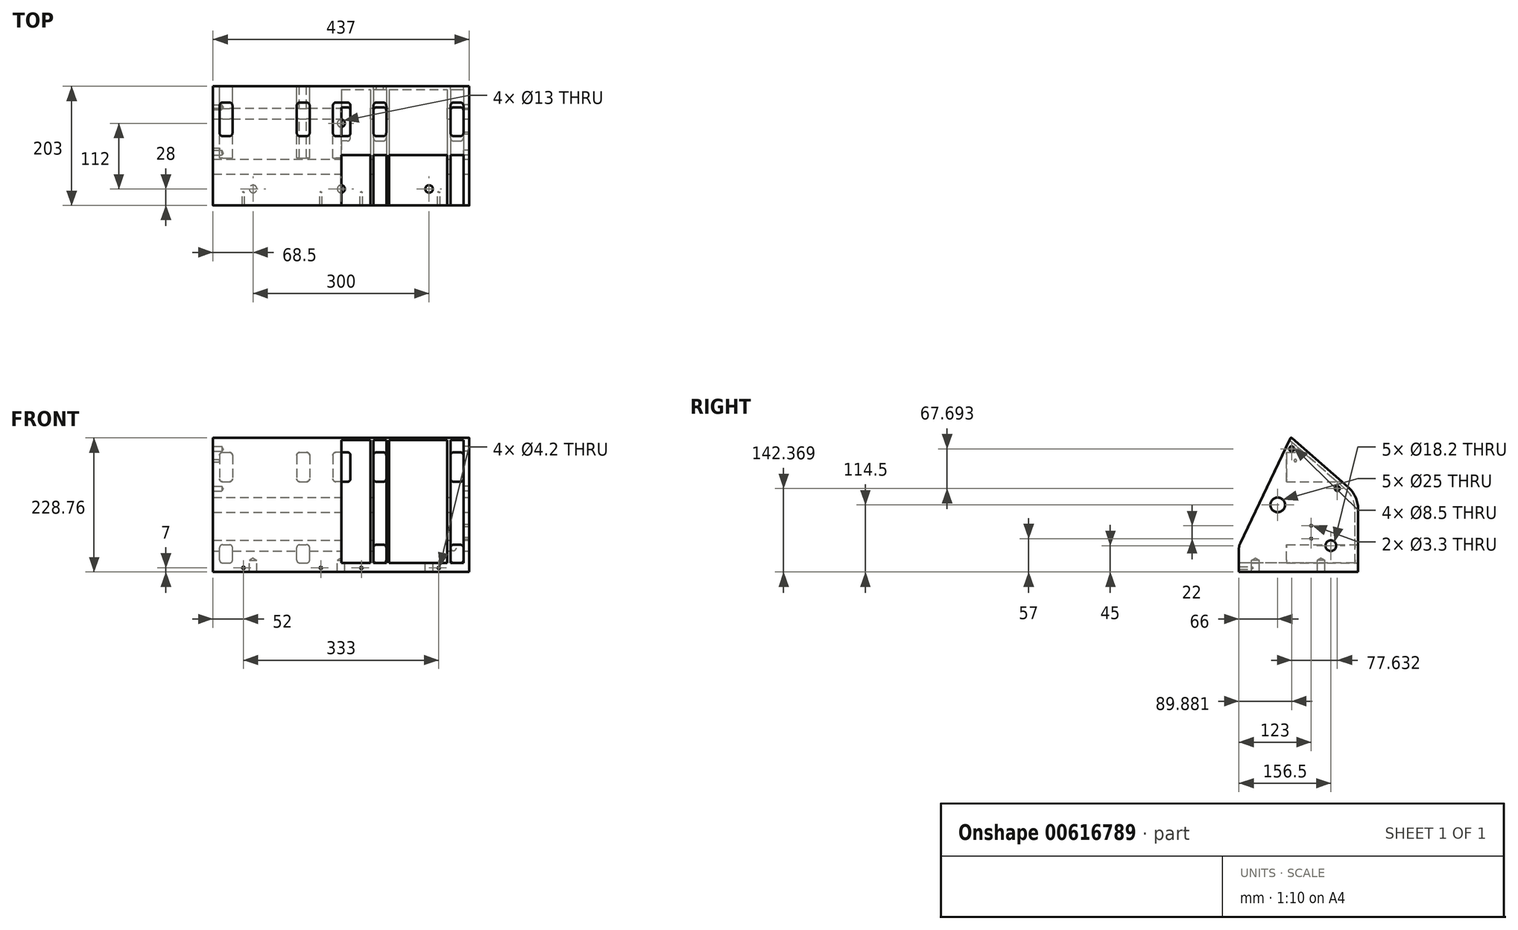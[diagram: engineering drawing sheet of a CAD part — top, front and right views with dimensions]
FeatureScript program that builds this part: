
annotation { "Feature Type Name" : "Feature", "Feature Type Description" : "" }
export const myFeature = defineFeature(function(context is Context, id is Id, definition is map)
    precondition{}
    {
        {
            var Q0;
            Q0=qCreatedBy(makeId("Right.planeOp"),FACE);
            var sketch = newSketch(context, id + "F0", { "sketchPlane" : qUnion([Q0])});
            skLineSegment(sketch, "E0", {"start": v(0, 0) * mm, "end": v(-203, 0) * mm});
            skLineSegment(sketch, "E1", {"start": v(-203, 0) * mm, "end": v(-203, 40.47) * mm});
            skLineSegment(sketch, "E2", {"start": v(0, 0) * mm, "end": v(0, 107.26) * mm});
            skLineSegment(sketch, "E3", {"start": v(-17.14, 144.95) * mm, "end": v(-112.7, 228.27) * mm});
            skLineSegment(sketch, "E4", {"start": v(-115.82, 227.62) * mm, "end": v(-201.05, 49.09) * mm});
            skPoint(sketch, "E5.visualSharp", {"position": v(0, 130) * mm});
            skArc(sketch, "E5.filletArc", {"start": v(0, 107.26) * mm, "mid": v(-4.49, 127.96) * mm, "end": v(-17.14, 144.95) * mm});
            skPoint(sketch, "E6.visualSharp", {"position": v(-203, 45) * mm});
            skArc(sketch, "E6.filletArc", {"start": v(-201.05, 49.09) * mm, "mid": v(-202.5, 44.89) * mm, "end": v(-203, 40.47) * mm});
            skPoint(sketch, "E7.visualSharp", {"position": v(-114.68, 230) * mm});
            skArc(sketch, "E7.filletArc", {"start": v(-112.7, 228.27) * mm, "mid": v(-114.42, 228.72) * mm, "end": v(-115.82, 227.62) * mm});
            skSolve(sketch);
        }
        {
            var Q0;
            Q0 = qSketchRegion(id + "F0", true);
            extrude(context, id + "F1", {"entities" : qUnion([Q0]), "oppositeDirection" : true, "depth" : 437 * mm, "offsetDistance" : 25 * mm});
        }
        {
            var Q0;
            Q0=makeQuery(id+"F1.opExtrude","CAP_FACE",FACE,{"disambiguationData":[OSD([sQuery(id+"F0.wireOp",EDGE,"E0"),sQuery(id+"F0.wireOp",EDGE,"E1"),sQuery(id+"F0.wireOp",EDGE,"E2"),sQuery(id+"F0.wireOp",EDGE,"E3"),sQuery(id+"F0.wireOp",EDGE,"E4"),sQuery(id+"F0.wireOp",EDGE,"E5.filletArc"),sQuery(id+"F0.wireOp",EDGE,"E6.filletArc"),sQuery(id+"F0.wireOp",EDGE,"E7.filletArc")])],"isStart":true});
            var sketch = newSketch(context, id + "F2", { "sketchPlane" : qUnion([Q0])});
            skLineSegment(sketch, "E8.0.0", {"start": v(-203, 0) * mm, "end": v(0, 0) * mm, "construction": true});
            skLineSegment(sketch, "E8.0.1", {"start": v(0, 0) * mm, "end": v(0, 107.26) * mm, "construction": true});
            skArc(sketch, "E8.0.2", {"start": v(0, 107.26) * mm, "mid": v(-4.49, 127.96) * mm, "end": v(-17.14, 144.95) * mm, "construction": true});
            skLineSegment(sketch, "E8.0.3", {"start": v(-17.14, 144.95) * mm, "end": v(-112.7, 228.27) * mm, "construction": true});
            skArc(sketch, "E8.0.4", {"start": v(-112.7, 228.27) * mm, "mid": v(-114.42, 228.72) * mm, "end": v(-115.82, 227.62) * mm, "construction": true});
            skLineSegment(sketch, "E8.0.5", {"start": v(-115.82, 227.62) * mm, "end": v(-201.05, 49.09) * mm, "construction": true});
            skArc(sketch, "E8.0.6", {"start": v(-201.05, 49.09) * mm, "mid": v(-202.5, 44.89) * mm, "end": v(-203, 40.47) * mm, "construction": true});
            skLineSegment(sketch, "E8.0.7", {"start": v(-203, 40.47) * mm, "end": v(-203, 0) * mm, "construction": true});
            skLineSegment(sketch, "E9.0", {"start": v(-197.5, 40.47) * mm, "end": v(-197.5, 15.5) * mm, "construction": true});
            skArc(sketch, "E9.1", {"start": v(-196.09, 46.72) * mm, "mid": v(-197.14, 43.67) * mm, "end": v(-197.5, 40.47) * mm, "construction": true});
            skLineSegment(sketch, "E9.2", {"start": v(-5.5, 5.5) * mm, "end": v(-5.5, 15.5) * mm, "construction": true});
            skArc(sketch, "E9.3", {"start": v(-5.5, 107.26) * mm, "mid": v(-9.5, 125.68) * mm, "end": v(-20.75, 140.8) * mm});
            skLineSegment(sketch, "E9.4", {"start": v(-20.75, 140.8) * mm, "end": v(-121.05, 228.26) * mm});
            skLineSegment(sketch, "E9.5", {"start": v(-197.5, 5.5) * mm, "end": v(-5.5, 5.5) * mm, "construction": true});
            skLineSegment(sketch, "E9.6", {"start": v(-112.84, 221.1) * mm, "end": v(-196.09, 46.72) * mm, "construction": true});
            skLineSegment(sketch, "E10", {"start": v(-197.5, 15.5) * mm, "end": v(-5.5, 15.5) * mm});
            skLineSegment(sketch, "E11", {"start": v(-197.5, 15.5) * mm, "end": v(-197.5, 5.5) * mm, "construction": true});
            skLineSegment(sketch, "E12", {"start": v(-5.5, 15.5) * mm, "end": v(-5.5, 107.26) * mm});
            skLineSegment(sketch, "E13.0", {"start": v(-208, 40.47) * mm, "end": v(-208, 15.5) * mm});
            skArc(sketch, "E13.1", {"start": v(-205.56, 51.24) * mm, "mid": v(-207.38, 46) * mm, "end": v(-208, 40.47) * mm});
            skLineSegment(sketch, "E13.2", {"start": v(-121.05, 228.26) * mm, "end": v(-205.56, 51.24) * mm});
            skLineSegment(sketch, "E14", {"start": v(-197.5, 15.5) * mm, "end": v(-208, 15.5) * mm});
            skLineSegment(sketch, "E15", {"start": v(-208, 15.5) * mm, "end": v(-208, 0) * mm, "construction": true});
            skSolve(sketch);
        }
        {
            var Q0;
            Q0 = qSketchRegion(id + "F2", true);
            extrude(context, id + "F3", {"entities" : qUnion([Q0]), "operationType" : NewBodyOperationType.REMOVE, "oppositeDirection" : true, "depth" : 32 * mm, "offsetDistance" : 25 * mm, "hasSecondDirection" : true, "secondDirectionOppositeDirection" : true, "secondDirectionDepth" : 10 * mm});
        }
        {
            var Q0;
            Q0 = qSketchRegion(id + "F2", true);
            extrude(context, id + "F4", {"entities" : qUnion([Q0]), "operationType" : NewBodyOperationType.REMOVE, "oppositeDirection" : true, "depth" : (((437 - (5 * 6) - 20 - (22 * 4)) / 3) + 15 + 22) * mm, "offsetDistance" : 25 * mm, "hasSecondDirection" : true, "secondDirectionOppositeDirection" : true, "secondDirectionDepth" : 38 * mm});
        }
        {
            var Q0;
            Q0 = qSketchRegion(id + "F2", true);
            extrude(context, id + "F5", {"entities" : qUnion([Q0]), "operationType" : NewBodyOperationType.REMOVE, "oppositeDirection" : true, "depth" : (141.5 + 22) * mm, "offsetDistance" : 25 * mm, "hasSecondDirection" : true, "secondDirectionOppositeDirection" : true, "secondDirectionDepth" : (10 + 23 + 5 + 98.5 + 5) * mm});
        }
        {
            var Q0;
            Q0 = qSketchRegion(id + "F2", true);
            extrude(context, id + "F6", {"entities" : qUnion([Q0]), "operationType" : NewBodyOperationType.REMOVE, "oppositeDirection" : true, "depth" : (163.5 + 5 + 98.67 / 2) * mm, "offsetDistance" : 25 * mm, "hasSecondDirection" : true, "secondDirectionOppositeDirection" : true, "secondDirectionDepth" : (163.5 + 5) * mm});
        }
        {
            var Q0;
            Q0=makeQuery(id+"F1.opExtrude","CAP_FACE",FACE,{"disambiguationData":[OSD([sQuery(id+"F0.wireOp",EDGE,"E0"),sQuery(id+"F0.wireOp",EDGE,"E1"),sQuery(id+"F0.wireOp",EDGE,"E2"),sQuery(id+"F0.wireOp",EDGE,"E3"),sQuery(id+"F0.wireOp",EDGE,"E4"),sQuery(id+"F0.wireOp",EDGE,"E5.filletArc"),sQuery(id+"F0.wireOp",EDGE,"E6.filletArc"),sQuery(id+"F0.wireOp",EDGE,"E7.filletArc")])],"isStart":true});
            var sketch = newSketch(context, id + "F7", { "sketchPlane" : qUnion([Q0])});
            skCircle(sketch, "E16", {"center": v(-46.5, 45) * mm, "radius": 9.1 * mm});
            skCircle(sketch, "E17", {"center": v(-137, 114.5) * mm, "radius": 12.5 * mm});
            skCircle(sketch, "E18", {"center": v(-80, 79) * mm, "radius": 2 * mm, "construction": true});
            skCircle(sketch, "E19", {"center": v(-80, 57) * mm, "radius": 2 * mm, "construction": true});
            skLineSegment(sketch, "E20", {"start": v(-80, 79) * mm, "end": v(-80, 57) * mm, "construction": true});
            skLineSegment(sketch, "E21", {"start": v(-80, 68) * mm, "end": v(0, 68) * mm, "construction": true});
            skSolve(sketch);
        }
        {
            var Q0;
            Q0=makeQuery(id+"F7.imprint","IMPRINT",FACE,{"disambiguationData":[TD([[makeQuery(id+"F7.imprint","IMPRINT",EDGE,{"derivedFrom":sQuery(id+"F7.wireOp",EDGE,"E17")}),1.0]])]});
            var Q1;
            Q1=makeQuery(id+"F7.imprint","IMPRINT",FACE,{"disambiguationData":[TD([[makeQuery(id+"F7.imprint","IMPRINT",EDGE,{"derivedFrom":sQuery(id+"F7.wireOp",EDGE,"E16")}),1.0]])]});
            extrude(context, id + "F8", {"entities" : qUnion([Q0, Q1]), "operationType" : NewBodyOperationType.REMOVE, "endBound" : BoundingType.THROUGH_ALL, "oppositeDirection" : true, "depth" : 25 * mm, "offsetDistance" : 25 * mm});
        }
        {
            var Q0;
            Q0=makeQuery(id+"F1.opExtrude","CAP_FACE",FACE,{"disambiguationData":[OSD([sQuery(id+"F0.wireOp",EDGE,"E0"),sQuery(id+"F0.wireOp",EDGE,"E1"),sQuery(id+"F0.wireOp",EDGE,"E2"),sQuery(id+"F0.wireOp",EDGE,"E3"),sQuery(id+"F0.wireOp",EDGE,"E4"),sQuery(id+"F0.wireOp",EDGE,"E5.filletArc"),sQuery(id+"F0.wireOp",EDGE,"E6.filletArc"),sQuery(id+"F0.wireOp",EDGE,"E7.filletArc")])],"isStart":false});
            var sketch = newSketch(context, id + "F9", { "sketchPlane" : qUnion([Q0])});
            skPoint(sketch, "E22", {"position": v(107, 190) * mm});
            skPoint(sketch, "E23", {"position": v(113.12, 210.06) * mm});
            skPoint(sketch, "E24", {"position": v(35.49, 142.37) * mm});
            skSolve(sketch);
        }
        {
            var Q0;
            Q0=makeQuery(id+"F1.opExtrude","CAP_FACE",FACE,{"disambiguationData":[OSD([sQuery(id+"F0.wireOp",EDGE,"E0"),sQuery(id+"F0.wireOp",EDGE,"E1"),sQuery(id+"F0.wireOp",EDGE,"E2"),sQuery(id+"F0.wireOp",EDGE,"E3"),sQuery(id+"F0.wireOp",EDGE,"E4"),sQuery(id+"F0.wireOp",EDGE,"E5.filletArc"),sQuery(id+"F0.wireOp",EDGE,"E6.filletArc"),sQuery(id+"F0.wireOp",EDGE,"E7.filletArc")])],"isStart":true});
            var sketch = newSketch(context, id + "F10", { "sketchPlane" : qUnion([Q0])});
            skPoint(sketch, "E25.0", {"position": v(-113.12, 210.06) * mm});
            skPoint(sketch, "E26.0", {"position": v(-35.49, 142.37) * mm});
            skSolve(sketch);
        }
        {
            var Q0;
            Q0=sQuery(id+"F7.wireOp",VERTEX,"E20.start");
            var Q1;
            Q1=sQuery(id+"F7.wireOp",VERTEX,"E20.end");
            var Q2;
            Q2=makeQuery(id+"F1.opExtrude","SWEPT_BODY",BODY,{"disambiguationData":[OSD([sQuery(id+"F0.wireOp",EDGE,"E0"),sQuery(id+"F0.wireOp",EDGE,"E1"),sQuery(id+"F0.wireOp",EDGE,"E2"),sQuery(id+"F0.wireOp",EDGE,"E3"),sQuery(id+"F0.wireOp",EDGE,"E4"),sQuery(id+"F0.wireOp",EDGE,"E5.filletArc"),sQuery(id+"F0.wireOp",EDGE,"E6.filletArc"),sQuery(id+"F0.wireOp",EDGE,"E7.filletArc")])]});
            hole(context, id + "F11", {"style" : HoleStyle.SIMPLE, "endStyle" : HoleEndStyle.BLIND, "standardTappedOrClearance" : lookupTablePath({ "standard" : "ISO", "engagement" : "75%", "pitch" : "0.7 mm", "size" : "M4", "type" : "Tapped" }), "standardBlindInLast" : lookupTablePath({ "standard" : "ISO", "fit" : "Normal", "engagement" : "75%", "pitch" : "0.7 mm", "size" : "M4", "type" : "Clearance & tapped" }), "holeDiameter" : 3.3 * mm, "majorDiameter" : 4 * mm, "showTappedDepth" : true, "holeDepth" : 14.1 * mm, "isTappedThrough" : true, "tappedDepth" : 12 * mm, "tapClearance" : 3, "locations" : qUnion([Q0, Q1]), "scope" : qUnion([Q2]), "startStyle" : HoleStartStyle.PART});
        }
        {
            var Q0;
            Q0=sQuery(id+"F9.wireOp",VERTEX,"E22");
            var Q1;
            Q1=makeQuery(id+"F1.opExtrude","SWEPT_BODY",BODY,{"disambiguationData":[OSD([sQuery(id+"F0.wireOp",EDGE,"E0"),sQuery(id+"F0.wireOp",EDGE,"E1"),sQuery(id+"F0.wireOp",EDGE,"E2"),sQuery(id+"F0.wireOp",EDGE,"E3"),sQuery(id+"F0.wireOp",EDGE,"E4"),sQuery(id+"F0.wireOp",EDGE,"E5.filletArc"),sQuery(id+"F0.wireOp",EDGE,"E6.filletArc"),sQuery(id+"F0.wireOp",EDGE,"E7.filletArc")])]});
            hole(context, id + "F12", {"style" : HoleStyle.SIMPLE, "endStyle" : HoleEndStyle.BLIND, "standardTappedOrClearance" : lookupTablePath({ "standard" : "ISO", "engagement" : "75%", "pitch" : "0.8 mm", "size" : "M5", "type" : "Tapped" }), "standardBlindInLast" : lookupTablePath({ "standard" : "ISO", "fit" : "Normal", "engagement" : "75%", "pitch" : "0.8 mm", "size" : "M5", "type" : "Clearance & tapped" }), "holeDiameter" : 4.2 * mm, "majorDiameter" : 5 * mm, "showTappedDepth" : true, "holeDepth" : 14.4 * mm, "isTappedThrough" : true, "tappedDepth" : 12 * mm, "tapClearance" : 3, "locations" : qUnion([Q0]), "scope" : qUnion([Q1]), "startStyle" : HoleStartStyle.PART});
        }
        {
            var Q0;
            Q0=sQuery(id+"F9.wireOp",VERTEX,"E24");
            var Q1;
            Q1=sQuery(id+"F9.wireOp",VERTEX,"E23");
            var Q2;
            Q2=sQuery(id+"F10.wireOp",VERTEX,"E26.0");
            var Q3;
            Q3=sQuery(id+"F10.wireOp",VERTEX,"E25.0");
            var Q4;
            Q4=makeQuery(id+"F1.opExtrude","SWEPT_BODY",BODY,{"disambiguationData":[OSD([sQuery(id+"F0.wireOp",EDGE,"E0"),sQuery(id+"F0.wireOp",EDGE,"E1"),sQuery(id+"F0.wireOp",EDGE,"E2"),sQuery(id+"F0.wireOp",EDGE,"E3"),sQuery(id+"F0.wireOp",EDGE,"E4"),sQuery(id+"F0.wireOp",EDGE,"E5.filletArc"),sQuery(id+"F0.wireOp",EDGE,"E6.filletArc"),sQuery(id+"F0.wireOp",EDGE,"E7.filletArc")])]});
            hole(context, id + "F13", {"style" : HoleStyle.SIMPLE, "endStyle" : HoleEndStyle.BLIND, "holeDiameter" : 8.5 * mm, "majorDiameter" : 5 * mm, "holeDepth" : 15 * mm, "isTappedThrough" : true, "tappedDepth" : 12 * mm, "tapClearance" : 3, "locations" : qUnion([Q0, Q1, Q2, Q3]), "scope" : qUnion([Q4]), "startStyle" : HoleStartStyle.PART});
        }
        {
            var Q0;
            Q0=makeQuery(id+"F1.opExtrude","SWEPT_FACE",FACE,{"disambiguationData":[OSD([sQuery(id+"F0.wireOp",EDGE,"E1")])]});
            var sketch = newSketch(context, id + "F14", { "sketchPlane" : qUnion([Q0])});
            skPoint(sketch, "E27", {"position": v(-385, 7) * mm});
            skPoint(sketch, "E28", {"position": v(-253, 7) * mm});
            skPoint(sketch, "E29", {"position": v(-184, 7) * mm});
            skPoint(sketch, "E30", {"position": v(-52, 7) * mm});
            skSolve(sketch);
        }
        {
            var Q0;
            Q0=sQuery(id+"F14.wireOp",VERTEX,"E27");
            var Q1;
            Q1=sQuery(id+"F14.wireOp",VERTEX,"E28");
            var Q2;
            Q2=sQuery(id+"F14.wireOp",VERTEX,"E29");
            var Q3;
            Q3=sQuery(id+"F14.wireOp",VERTEX,"E30");
            var Q4;
            Q4=makeQuery(id+"F1.opExtrude","SWEPT_BODY",BODY,{"disambiguationData":[OSD([sQuery(id+"F0.wireOp",EDGE,"E0"),sQuery(id+"F0.wireOp",EDGE,"E1"),sQuery(id+"F0.wireOp",EDGE,"E2"),sQuery(id+"F0.wireOp",EDGE,"E3"),sQuery(id+"F0.wireOp",EDGE,"E4"),sQuery(id+"F0.wireOp",EDGE,"E5.filletArc"),sQuery(id+"F0.wireOp",EDGE,"E6.filletArc"),sQuery(id+"F0.wireOp",EDGE,"E7.filletArc")])]});
            hole(context, id + "F15", {"style" : HoleStyle.SIMPLE, "endStyle" : HoleEndStyle.BLIND, "standardTappedOrClearance" : lookupTablePath({ "standard" : "ISO", "engagement" : "75%", "pitch" : "0.8 mm", "size" : "M5", "type" : "Tapped" }), "standardBlindInLast" : lookupTablePath({ "fit" : "Normal", "standard" : "ISO", "engagement" : "75%", "pitch" : "0.8 mm", "size" : "M5", "type" : "Clearance & tapped" }), "holeDiameter" : 4.2 * mm, "majorDiameter" : 5 * mm, "showTappedDepth" : true, "holeDepth" : 22.4 * mm, "isTappedThrough" : true, "tappedDepth" : 20 * mm, "tapClearance" : 3, "locations" : qUnion([Q0, Q1, Q2, Q3]), "scope" : qUnion([Q4]), "startStyle" : HoleStartStyle.PART});
        }
        {
            var Q0;
            Q0=makeQuery(id+"F1.opExtrude","SWEPT_FACE",FACE,{"disambiguationData":[OSD([sQuery(id+"F0.wireOp",EDGE,"E0")])]});
            var sketch = newSketch(context, id + "F16", { "sketchPlane" : qUnion([Q0])});
            skPoint(sketch, "E31", {"position": v(-368.5, 175) * mm});
            skPoint(sketch, "E32", {"position": v(-218.5, 175) * mm});
            skPoint(sketch, "E33", {"position": v(-68.5, 175) * mm});
            skPoint(sketch, "E34", {"position": v(-218.5, 63) * mm});
            skLineSegment(sketch, "E35", {"start": v(-218.5, 203) * mm, "end": v(-218.5, 0) * mm, "construction": true});
            skSolve(sketch);
        }
        {
            var Q0;
            Q0=sQuery(id+"F16.wireOp",VERTEX,"E31");
            var Q1;
            Q1=sQuery(id+"F16.wireOp",VERTEX,"E32");
            var Q2;
            Q2=sQuery(id+"F16.wireOp",VERTEX,"E33");
            var Q3;
            Q3=sQuery(id+"F16.wireOp",VERTEX,"E34");
            var Q4;
            Q4=makeQuery(id+"F1.opExtrude","SWEPT_BODY",BODY,{"disambiguationData":[OSD([sQuery(id+"F0.wireOp",EDGE,"E0"),sQuery(id+"F0.wireOp",EDGE,"E1"),sQuery(id+"F0.wireOp",EDGE,"E2"),sQuery(id+"F0.wireOp",EDGE,"E3"),sQuery(id+"F0.wireOp",EDGE,"E4"),sQuery(id+"F0.wireOp",EDGE,"E5.filletArc"),sQuery(id+"F0.wireOp",EDGE,"E6.filletArc"),sQuery(id+"F0.wireOp",EDGE,"E7.filletArc")])]});
            hole(context, id + "F17", {"style" : HoleStyle.SIMPLE, "endStyle" : HoleEndStyle.BLIND, "holeDiameter" : 13 * mm, "majorDiameter" : 5 * mm, "holeDepth" : 20 * mm, "isTappedThrough" : true, "tappedDepth" : 20 * mm, "tapClearance" : 3, "locations" : qUnion([Q0, Q1, Q2, Q3]), "scope" : qUnion([Q4]), "startStyle" : HoleStartStyle.PART});
        }
        {
            var Q0;
            Q0=makeQuery(id+"F1.opExtrude","SWEPT_FACE",FACE,{"disambiguationData":[OSD([sQuery(id+"F0.wireOp",EDGE,"E2")])]});
            var sketch = newSketch(context, id + "F18", { "sketchPlane" : qUnion([Q0])});
            skLineSegment(sketch, "E36.0", {"start": v(299, 15.5) * mm, "end": v(397.67, 15.5) * mm, "construction": true});
            skLineSegment(sketch, "E37.bottom", {"start": v(420.67, 15.5) * mm, "end": v(408.67, 15.5) * mm});
            skLineSegment(sketch, "E37.top", {"start": v(420.67, 46.5) * mm, "end": v(408.67, 46.5) * mm});
            skLineSegment(sketch, "E37.left", {"start": v(425.67, 20.5) * mm, "end": v(425.67, 41.5) * mm});
            skLineSegment(sketch, "E37.right", {"start": v(403.67, 20.5) * mm, "end": v(403.67, 41.5) * mm});
            skLineSegment(sketch, "E38", {"start": v(414.67, 46.5) * mm, "end": v(414.67, 15.5) * mm, "construction": true});
            skLineSegment(sketch, "E39.0", {"start": v(425.67, 224.85) * mm, "end": v(425.67, 49.09) * mm, "construction": true});
            skPoint(sketch, "E40.visualSharp", {"position": v(403.67, 46.5) * mm});
            skArc(sketch, "E40.filletArc", {"start": v(408.67, 46.5) * mm, "mid": v(405.13, 45.04) * mm, "end": v(403.67, 41.5) * mm});
            skPoint(sketch, "E41.visualSharp", {"position": v(425.67, 46.5) * mm});
            skArc(sketch, "E41.filletArc", {"start": v(425.67, 41.5) * mm, "mid": v(424.2, 45.04) * mm, "end": v(420.67, 46.5) * mm});
            skPoint(sketch, "E42.visualSharp", {"position": v(425.67, 15.5) * mm});
            skArc(sketch, "E42.filletArc", {"start": v(420.67, 15.5) * mm, "mid": v(424.2, 16.96) * mm, "end": v(425.67, 20.5) * mm});
            skPoint(sketch, "E43.visualSharp", {"position": v(403.67, 15.5) * mm});
            skArc(sketch, "E43.filletArc", {"start": v(403.67, 20.5) * mm, "mid": v(405.13, 16.96) * mm, "end": v(408.67, 15.5) * mm});
            skLineSegment(sketch, "E44.1.0.0", {"start": v(289.44, 46.5) * mm, "end": v(277.44, 46.5) * mm});
            skArc(sketch, "E44.1.0.1", {"start": v(277.44, 46.5) * mm, "mid": v(273.73, 45.14) * mm, "end": v(272.17, 41.5) * mm});
            skLineSegment(sketch, "E44.1.0.2", {"start": v(272.17, 20.5) * mm, "end": v(272.17, 41.5) * mm});
            skArc(sketch, "E44.1.0.3", {"start": v(272.17, 20.5) * mm, "mid": v(273.63, 16.96) * mm, "end": v(277.17, 15.5) * mm});
            skLineSegment(sketch, "E44.1.0.4", {"start": v(289.17, 15.5) * mm, "end": v(277.17, 15.5) * mm});
            skArc(sketch, "E44.1.0.5", {"start": v(289.17, 15.5) * mm, "mid": v(292.7, 16.96) * mm, "end": v(294.17, 20.5) * mm});
            skLineSegment(sketch, "E44.1.0.6", {"start": v(294.17, 20.5) * mm, "end": v(294.17, 41.5) * mm});
            skArc(sketch, "E44.1.0.7", {"start": v(294.17, 41.5) * mm, "mid": v(292.8, 44.94) * mm, "end": v(289.44, 46.5) * mm});
            skLineSegment(sketch, "E44.2.0.0", {"start": v(158.22, 46.5) * mm, "end": v(146.22, 46.5) * mm});
            skArc(sketch, "E44.2.0.1", {"start": v(146.22, 46.5) * mm, "mid": v(142.86, 44.94) * mm, "end": v(141.5, 41.5) * mm});
            skLineSegment(sketch, "E44.2.0.2", {"start": v(141.5, 20.5) * mm, "end": v(141.5, 41.5) * mm});
            skArc(sketch, "E44.2.0.3", {"start": v(141.5, 20.5) * mm, "mid": v(142.86, 17.06) * mm, "end": v(146.22, 15.5) * mm});
            skLineSegment(sketch, "E44.2.0.4", {"start": v(158.5, 15.5) * mm, "end": v(146.22, 15.5) * mm});
            skArc(sketch, "E44.2.0.5", {"start": v(158.5, 15.5) * mm, "mid": v(162.04, 16.96) * mm, "end": v(163.5, 20.5) * mm});
            skLineSegment(sketch, "E44.2.0.6", {"start": v(163.5, 20.5) * mm, "end": v(163.5, 41.5) * mm});
            skArc(sketch, "E44.2.0.7", {"start": v(163.5, 41.5) * mm, "mid": v(161.94, 45.14) * mm, "end": v(158.22, 46.5) * mm});
            skLineSegment(sketch, "E44.3.0.0", {"start": v(27, 46.5) * mm, "end": v(15, 46.5) * mm});
            skArc(sketch, "E44.3.0.1", {"start": v(15, 46.5) * mm, "mid": v(11.46, 45.04) * mm, "end": v(10, 41.5) * mm});
            skLineSegment(sketch, "E44.3.0.2", {"start": v(10, 20.5) * mm, "end": v(10, 41.5) * mm});
            skArc(sketch, "E44.3.0.3", {"start": v(10, 20.5) * mm, "mid": v(11.46, 16.96) * mm, "end": v(15, 15.5) * mm});
            skLineSegment(sketch, "E44.3.0.4", {"start": v(27, 15.5) * mm, "end": v(15, 15.5) * mm});
            skArc(sketch, "E44.3.0.5", {"start": v(27, 15.5) * mm, "mid": v(30.54, 16.96) * mm, "end": v(32, 20.5) * mm});
            skLineSegment(sketch, "E44.3.0.6", {"start": v(32, 20.5) * mm, "end": v(32, 41.5) * mm});
            skArc(sketch, "E44.3.0.7", {"start": v(32, 41.5) * mm, "mid": v(30.54, 45.04) * mm, "end": v(27, 46.5) * mm});
            skLineSegment(sketch, "E44.direction1", {"start": v(408.67, 46.5) * mm, "end": v(277.44, 46.5) * mm, "construction": true});
            skLineSegment(sketch, "E45.0", {"start": v(10, 49.09) * mm, "end": v(10, 224.85) * mm, "construction": true});
            skLineSegment(sketch, "E46.bottom", {"start": v(420.67, 204) * mm, "end": v(408.67, 204) * mm});
            skLineSegment(sketch, "E46.top", {"start": v(420.67, 154) * mm, "end": v(408.67, 154) * mm});
            skLineSegment(sketch, "E46.left", {"start": v(425.67, 199) * mm, "end": v(425.67, 159) * mm});
            skLineSegment(sketch, "E46.right", {"start": v(403.67, 199) * mm, "end": v(403.67, 159) * mm});
            skPoint(sketch, "E47.visualSharp", {"position": v(403.67, 204) * mm});
            skArc(sketch, "E47.filletArc", {"start": v(408.67, 204) * mm, "mid": v(405.13, 202.54) * mm, "end": v(403.67, 199) * mm});
            skPoint(sketch, "E48.visualSharp", {"position": v(403.67, 154) * mm});
            skArc(sketch, "E48.filletArc", {"start": v(403.67, 159) * mm, "mid": v(405.13, 155.46) * mm, "end": v(408.67, 154) * mm});
            skPoint(sketch, "E49.visualSharp", {"position": v(425.67, 204) * mm});
            skArc(sketch, "E49.filletArc", {"start": v(425.67, 199) * mm, "mid": v(424.2, 202.54) * mm, "end": v(420.67, 204) * mm});
            skPoint(sketch, "E50.visualSharp", {"position": v(425.67, 154) * mm});
            skArc(sketch, "E50.filletArc", {"start": v(420.67, 154) * mm, "mid": v(424.2, 155.46) * mm, "end": v(425.67, 159) * mm});
            skLineSegment(sketch, "E51.1.0.0", {"start": v(289.44, 204) * mm, "end": v(277.44, 204) * mm});
            skArc(sketch, "E51.1.0.1", {"start": v(277.44, 204) * mm, "mid": v(273.73, 202.64) * mm, "end": v(272.17, 199) * mm});
            skLineSegment(sketch, "E51.1.0.2", {"start": v(272.17, 199) * mm, "end": v(272.17, 159) * mm});
            skArc(sketch, "E51.1.0.3", {"start": v(272.17, 159) * mm, "mid": v(273.63, 155.46) * mm, "end": v(277.17, 154) * mm});
            skLineSegment(sketch, "E51.1.0.4", {"start": v(289.17, 154) * mm, "end": v(277.17, 154) * mm});
            skArc(sketch, "E51.1.0.5", {"start": v(289.17, 154) * mm, "mid": v(292.7, 155.46) * mm, "end": v(294.17, 159) * mm});
            skArc(sketch, "E51.1.0.6", {"start": v(294.17, 199) * mm, "mid": v(292.8, 202.44) * mm, "end": v(289.44, 204) * mm});
            skLineSegment(sketch, "E51.1.0.7", {"start": v(294.17, 199) * mm, "end": v(294.17, 159) * mm});
            skLineSegment(sketch, "E51.2.0.0", {"start": v(158.5, 204) * mm, "end": v(146.5, 204) * mm});
            skArc(sketch, "E51.2.0.1", {"start": v(146.5, 204) * mm, "mid": v(142.96, 202.54) * mm, "end": v(141.5, 199) * mm});
            skLineSegment(sketch, "E51.2.0.2", {"start": v(141.5, 199) * mm, "end": v(141.5, 159) * mm});
            skArc(sketch, "E51.2.0.3", {"start": v(141.5, 159) * mm, "mid": v(142.96, 155.46) * mm, "end": v(146.5, 154) * mm});
            skLineSegment(sketch, "E51.2.0.4", {"start": v(158.5, 154) * mm, "end": v(146.5, 154) * mm});
            skArc(sketch, "E51.2.0.5", {"start": v(158.5, 154) * mm, "mid": v(162.04, 155.46) * mm, "end": v(163.5, 159) * mm});
            skArc(sketch, "E51.2.0.6", {"start": v(163.5, 199) * mm, "mid": v(162.04, 202.54) * mm, "end": v(158.5, 204) * mm});
            skLineSegment(sketch, "E51.2.0.7", {"start": v(163.5, 199) * mm, "end": v(163.5, 159) * mm});
            skLineSegment(sketch, "E51.3.0.0", {"start": v(27, 204) * mm, "end": v(15, 204) * mm});
            skArc(sketch, "E51.3.0.1", {"start": v(15, 204) * mm, "mid": v(11.46, 202.54) * mm, "end": v(10, 199) * mm});
            skLineSegment(sketch, "E51.3.0.2", {"start": v(10, 199) * mm, "end": v(10, 159) * mm});
            skArc(sketch, "E51.3.0.3", {"start": v(10, 159) * mm, "mid": v(11.46, 155.46) * mm, "end": v(15, 154) * mm});
            skLineSegment(sketch, "E51.3.0.4", {"start": v(27, 154) * mm, "end": v(15, 154) * mm});
            skArc(sketch, "E51.3.0.5", {"start": v(27, 154) * mm, "mid": v(30.54, 155.46) * mm, "end": v(32, 159) * mm});
            skArc(sketch, "E51.3.0.6", {"start": v(32, 199) * mm, "mid": v(30.54, 202.54) * mm, "end": v(27, 204) * mm});
            skLineSegment(sketch, "E51.3.0.7", {"start": v(32, 199) * mm, "end": v(32, 159) * mm});
            skLineSegment(sketch, "E51.direction1", {"start": v(408.67, 204) * mm, "end": v(277.44, 204) * mm, "construction": true});
            skLineSegment(sketch, "E52.bottom", {"start": v(207.56, 204) * mm, "end": v(227.56, 204) * mm});
            skLineSegment(sketch, "E52.top", {"start": v(207.56, 154) * mm, "end": v(227.56, 154) * mm});
            skLineSegment(sketch, "E52.left", {"start": v(202.56, 199) * mm, "end": v(202.56, 159) * mm});
            skLineSegment(sketch, "E52.right", {"start": v(232.56, 199) * mm, "end": v(232.56, 159) * mm});
            skPoint(sketch, "E53.visualSharp", {"position": v(202.56, 204) * mm});
            skArc(sketch, "E53.filletArc", {"start": v(207.56, 204) * mm, "mid": v(204.02, 202.54) * mm, "end": v(202.56, 199) * mm});
            skPoint(sketch, "E54.visualSharp", {"position": v(232.56, 204) * mm});
            skArc(sketch, "E54.filletArc", {"start": v(232.56, 199) * mm, "mid": v(231.1, 202.54) * mm, "end": v(227.56, 204) * mm});
            skPoint(sketch, "E55.visualSharp", {"position": v(232.56, 154) * mm});
            skArc(sketch, "E55.filletArc", {"start": v(227.56, 154) * mm, "mid": v(231.1, 155.46) * mm, "end": v(232.56, 159) * mm});
            skPoint(sketch, "E56.visualSharp", {"position": v(202.56, 154) * mm});
            skArc(sketch, "E56.filletArc", {"start": v(202.56, 159) * mm, "mid": v(204.02, 155.46) * mm, "end": v(207.56, 154) * mm});
            skLineSegment(sketch, "E57.0", {"start": v(294.17, 224.85) * mm, "end": v(294.17, 49.09) * mm, "construction": true});
            skSolve(sketch);
        }
        {
            var Q0;
            Q0 = qSketchRegion(id + "F18", true);
            extrude(context, id + "F19", {"entities" : qUnion([Q0]), "operationType" : NewBodyOperationType.REMOVE, "oppositeDirection" : true, "depth" : 122 * mm, "offsetDistance" : 25 * mm});
        }
    });
